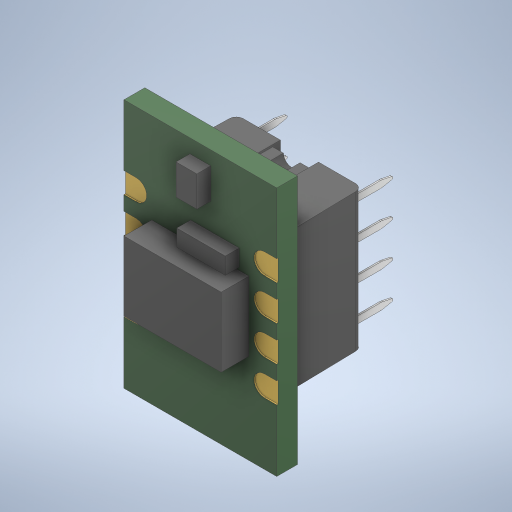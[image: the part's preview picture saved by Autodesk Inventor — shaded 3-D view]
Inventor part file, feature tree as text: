
AUTODESK INVENTOR PART (.ipt)
format: ipt  version: 2024.1 (Build 281209000, 209)  size: 1,592,832 bytes
history: native  units: mm
features: extrude x5, sketch x4, other x1, imported_body x1
ambient origin geometry x8: Origin, YZ Plane, XZ Plane, XY Plane, X Axis, Y Axis, Z Axis, Center Point
bodies: Body1 (feature_tree)
feature tree (11):
  other  "ソリッド1"
  extrude  "押し出し1"  Depth=1.5mm TaperAngle=0.0deg
  extrude  "押し出し2"  Depth=11.0mm
  sketch  "スケッチ3"
  extrude  "押し出し3"  Depth=18.0mm
  extrude  "押し出し4"  Depth=1.5mm TaperAngle=0.0deg
  extrude  "押し出し5"  Depth=2.0mm
  sketch  "スケッチ1"
  sketch  "スケッチ2"
  sketch  "スケッチ4"
  imported_body  "Base1"
